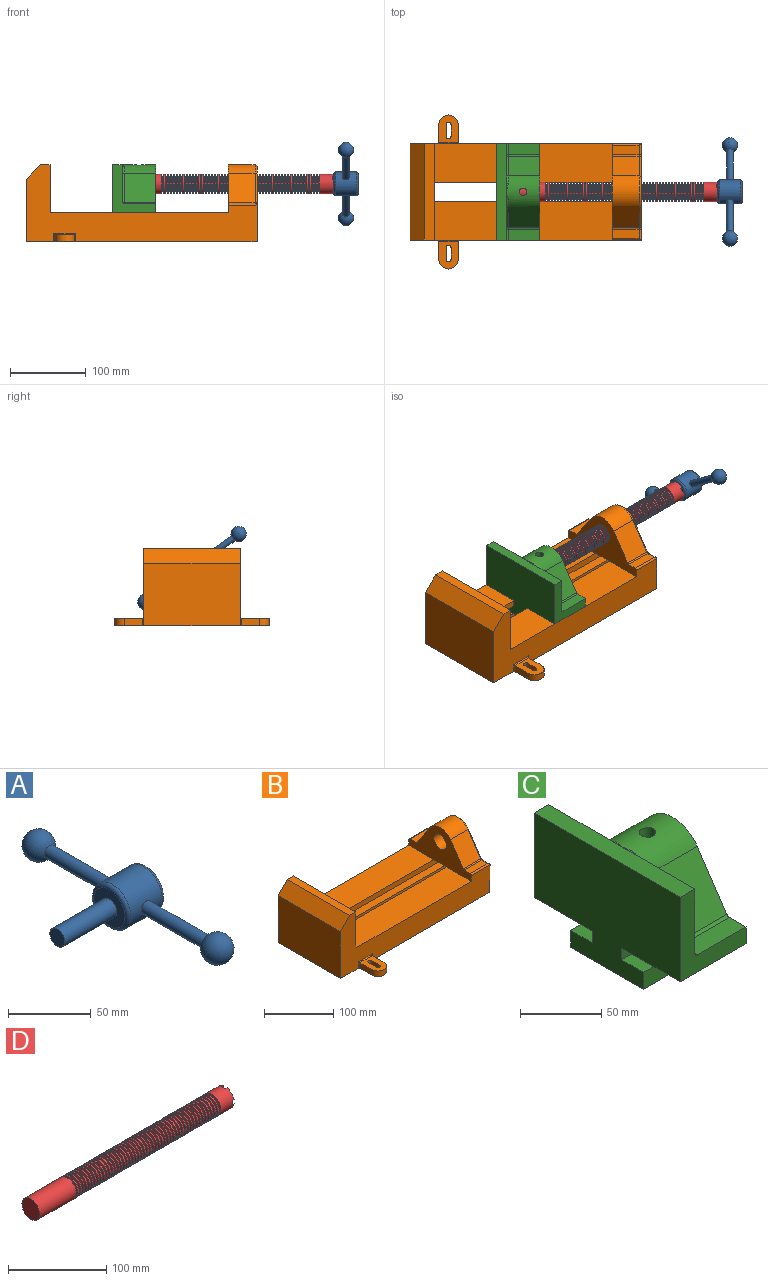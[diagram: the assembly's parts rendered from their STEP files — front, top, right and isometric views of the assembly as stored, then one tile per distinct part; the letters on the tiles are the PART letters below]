
ASSEMBLY  parts=4 mates=4
PART A: 11 faces, bbox 76.2x172.7x34.4 mm
  f0: sphere r=10.16mm, area 1231.8mm2, adj f1
  f1: cylinder r=4.45mm len=51.82mm, axis (0,1,0), area 1438.5mm2, adj f0,f4
  f2: sphere r=10.16mm, area 1231.8mm2, adj f3
  f3: cylinder r=4.45mm len=51.82mm, axis (0,1,0), area 1438.5mm2, adj f2,f4
  f4: cylinder r=15.88mm len=31.75mm, axis (-1,0,0), area 2534.7mm2, adj f1,f3,f9,f10
  f5: cylinder r=6.35mm len=44.45mm, axis (-1,0,0), area 1773.5mm2, adj f6,f8
  f6: plane 12.7x12.7mm, normal (-1,0,0), area 126.7mm2, adj f5
  f7: plane 26.67x26.67mm, normal (1,0,0), area 558.6mm2, adj f10
  f8: plane 26.67x26.67mm, normal (-1,0,0), area 432mm2, adj f5,f9
  f9: torus R=13.33mm, axis (1,0,0), area 374.8mm2, adj f4,f8
  f10: torus R=13.33mm, axis (1,0,0), area 374.8mm2, adj f4,f7
PART B: 61 faces, bbox 304.8x203.2x103.7 mm
  f0: plane 304.8x101.6mm, normal (0,1,0), area 13520.3mm2, adj f3,f4,f5,f6,f7,f8,f9,f16
  f1: plane 304.8x101.6mm, normal (0,-1,0), area 13520.3mm2, adj f2,f3,f5,f6,f7,f8,f9,f16
  f2: plane 234.95x50.8mm, normal (0,0,1), area 11935.5mm2, adj f1,f5,f16,f26
  f3: plane 127x99.06mm, normal (1,0,0), area 7097.5mm2, adj f0,f1,f9,f14,f17,f18,f19,f20
  f4: plane 234.95x50.8mm, normal (0,0,1), area 11935.5mm2, adj f0,f5,f16,f27
  f5: plane 127x101.6mm, normal (1,0,0), area 9516.1mm2, adj f0,f1,f2,f4,f6,f9,f18,f19
  f6: plane 127x12.7mm, normal (0,0,1), area 1612.9mm2, adj f0,f1,f5,f7
  f7: plane 127x19.05mm, normal (-0.71,0,0.71), area 3421.5mm2, adj f0,f1,f6,f8
  f8: plane 127x82.55mm, normal (-1,0,0), area 10483.8mm2, adj f0,f1,f7,f9
  f9: plane 304.8x203.2mm, normal (0,0,-1), area 33298.3mm2, adj f0,f1,f3,f5,f8,f21,f22,f39
  f10: plane 35.56x11.98mm, normal (0,0,1), area 426mm2, adj f16,f28,f29,f30
  f11: plane 38.43x35.56mm, normal (0,0.83,0.56), area 1645.4mm2, adj f12,f16,f29,f32
  f12: cylinder r=25.4mm len=42.19mm, axis (1,0,0), area 1770.2mm2, adj f11,f13,f16,f33
  f13: plane 38.43x35.56mm, normal (0,-0.83,0.56), area 1645.4mm2, adj f12,f16,f34,f35
  f14: cylinder r=12.7mm len=38.1mm, axis (1,0,0), area 3040.2mm2, adj f3,f16
  f15: plane 35.56x11.98mm, normal (0,0,1), area 426mm2, adj f16,f34,f36,f38
  f16: plane 127x63.5mm, normal (-1,0,0), area 4155.5mm2, adj f0,f1,f2,f4,f10,f11,f12,f13
  f17: plane 38.1x25.4mm, normal (0,0,-1), area 967.7mm2, adj f3,f16,f26,f27
  f18: plane 273.05x19.05mm, normal (0,0,-1), area 5201.6mm2, adj f3,f5,f19,f26
  f19: plane 273.05x12.7mm, normal (0,1,0), area 3467.7mm2, adj f3,f5,f18,f20
  f20: plane 273.05x19.05mm, normal (0,0,1), area 5201.6mm2, adj f3,f5,f19,f21
  f21: plane 273.05x16.51mm, normal (0,1,0), area 4508.1mm2, adj f3,f5,f9,f20
  f22: plane 273.05x16.51mm, normal (0,-1,0), area 4508.1mm2, adj f3,f5,f9,f23
  f23: plane 273.05x19.05mm, normal (0,0,1), area 5201.6mm2, adj f3,f5,f22,f24
  f24: plane 273.05x12.7mm, normal (0,-1,0), area 3467.7mm2, adj f3,f5,f23,f25
  f25: plane 273.05x19.05mm, normal (0,0,-1), area 5201.6mm2, adj f3,f5,f24,f27
  f26: plane 273.05x8.89mm, normal (0,1,0), area 2427.4mm2, adj f2,f3,f5,f17,f18
  f27: plane 273.05x8.89mm, normal (0,-1,0), area 2427.4mm2, adj f3,f4,f5,f17,f25
  f28: cylinder r=2.54mm len=38.1mm, axis (1,0,0), area 148.3mm2, adj f0,f10,f16,f30
  f29: cylinder r=2.54mm len=35.56mm, axis (-1,0,0), area 88.5mm2, adj f10,f11,f16,f31
  f30: cylinder r=2.54mm len=14.52mm, axis (0,1,0), area 54.3mm2, adj f3,f10,f28,f31
  f31: torus R=5.08mm, axis (-1,0,0), area 13.5mm2, adj f3,f29,f30,f32
  f32: cylinder r=2.54mm len=39.84mm, axis (0,0.56,-0.83), area 184.6mm2, adj f3,f11,f31,f33
  f33: torus R=22.86mm, axis (-1,0,0), area 191.4mm2, adj f3,f12,f32,f35
  f34: cylinder r=2.54mm len=35.56mm, axis (-1,0,0), area 88.5mm2, adj f13,f15,f16,f37
  f35: cylinder r=2.54mm len=39.84mm, axis (0,0.56,0.83), area 184.6mm2, adj f3,f13,f33,f37
  f36: cylinder r=2.54mm len=38.1mm, axis (-1,0,0), area 148.3mm2, adj f1,f15,f16,f38
  f37: torus R=5.08mm, axis (-1,0,0), area 13.5mm2, adj f3,f34,f35,f38
  f38: cylinder r=2.54mm len=14.52mm, axis (0,1,0), area 54.3mm2, adj f3,f15,f36,f37
  f39: plane 23.88x9.53mm, normal (-1,0,0), area 227.4mm2, adj f9,f45,f46,f60
  f40: plane 23.88x9.53mm, normal (1,0,0), area 227.4mm2, adj f9,f45,f46,f58
  f41: cylinder r=3.3mm len=9.53mm, axis (0,0,-1), area 98.8mm2, adj f9,f42,f44,f46
  f42: plane 15.62x9.53mm, normal (-1,0,0), area 148.8mm2, adj f9,f41,f43,f46
  f43: cylinder r=3.3mm len=9.53mm, axis (0,0,-1), area 98.8mm2, adj f9,f42,f44,f46
  f44: plane 15.62x9.53mm, normal (1,0,0), area 148.8mm2, adj f9,f41,f43,f46
  f45: cylinder r=12.7mm len=25.4mm, axis (0,0,-1), area 380mm2, adj f9,f39,f40,f46
  f46: plane 36.58x25.4mm, normal (0,0,1), area 722.4mm2, adj f39,f40,f41,f42,f43,f44,f45,f59
  f47: plane 23.88x9.53mm, normal (-1,0,0), area 227.4mm2, adj f9,f53,f54,f56
  f48: plane 23.88x9.53mm, normal (1,0,0), area 227.4mm2, adj f9,f53,f54,f55
  f49: cylinder r=3.3mm len=9.53mm, axis (0,0,-1), area 98.8mm2, adj f9,f50,f52,f54
  f50: plane 15.62x9.53mm, normal (-1,0,0), area 148.8mm2, adj f9,f49,f51,f54
  f51: cylinder r=3.3mm len=9.53mm, axis (0,0,-1), area 98.8mm2, adj f9,f50,f52,f54
  f52: plane 15.62x9.53mm, normal (1,0,0), area 148.8mm2, adj f9,f49,f51,f54
  f53: cylinder r=12.7mm len=25.4mm, axis (0,0,-1), area 380mm2, adj f9,f47,f48,f54
  f54: plane 36.58x25.4mm, normal (0,0,1), area 722.4mm2, adj f47,f48,f49,f50,f51,f52,f53,f57
  f55: cylinder r=1.52mm len=11.05mm, axis (0,0,-1), area 24.1mm2, adj f0,f9,f48,f57
  f56: cylinder r=1.52mm len=11.05mm, axis (0,0,1), area 24.1mm2, adj f0,f9,f47,f57
  f57: cylinder r=1.52mm len=28.45mm, axis (1,0,0), area 63.5mm2, adj f0,f54,f55,f56
  f58: cylinder r=1.52mm len=11.05mm, axis (0,0,1), area 24.1mm2, adj f1,f9,f40,f59
  f59: cylinder r=1.52mm len=28.45mm, axis (-1,0,0), area 63.5mm2, adj f1,f46,f58,f60
  f60: cylinder r=1.52mm len=11.05mm, axis (0,0,-1), area 24.1mm2, adj f1,f9,f39,f59
PART C: 36 faces, bbox 57.2x127x89 mm
  f0: plane 57.15x50.8mm, normal (0,0,-1), area 2903.2mm2, adj f6,f9,f10,f23
  f1: cylinder r=12.7mm len=44.45mm, axis (1,0,0), area 3464.3mm2, adj f6,f15,f16
  f2: plane 41.91x14.52mm, normal (0,0,1), area 608.5mm2, adj f6,f11,f24,f25
  f3: plane 51.86x48.26mm, normal (1,0,0), area 1495.7mm2, adj f8,f10,f31,f33,f35
  f4: plane 51.86x48.26mm, normal (1,0,0), area 1495.7mm2, adj f8,f11,f24,f28,f29
  f5: plane 57.15x50.8mm, normal (0,0,-1), area 2903.2mm2, adj f6,f9,f11,f22
  f6: plane 127x85.09mm, normal (1,0,0), area 5190.6mm2, adj f0,f1,f2,f5,f7,f10,f11,f12
  f7: plane 41.91x14.52mm, normal (0,0,1), area 608.5mm2, adj f6,f10,f30,f31
  f8: plane 127x12.7mm, normal (0,0,1), area 1612.9mm2, adj f3,f4,f9,f10,f11,f26,f34
  f9: plane 127x85.09mm, normal (-1,0,0), area 9096.8mm2, adj f0,f5,f8,f10,f11,f17,f18,f19
  f10: plane 63.5x57.15mm, normal (0,-1,0), area 1372.3mm2, adj f0,f3,f6,f7,f8,f9,f31
  f11: plane 63.5x57.15mm, normal (0,1,0), area 1372.3mm2, adj f2,f4,f5,f6,f8,f9,f24
  f12: plane 41.91x38.43mm, normal (0,-0.83,0.56), area 1939.2mm2, adj f6,f13,f30,f33
  f13: cylinder r=25.4mm len=44.45mm, axis (1,0,0), area 2026.5mm2, adj f6,f12,f14,f16,f26,f28,f34,f35
  f14: plane 41.91x38.43mm, normal (0,0.83,0.56), area 1939.2mm2, adj f6,f13,f25,f29
  f15: plane 25.4x25.4mm, normal (1,0,0), area 506.7mm2, adj f1
  f16: cylinder r=5.08mm len=13.76mm, axis (0,0,1), area 414mm2, adj f1,f13
  f17: plane 57.15x19.05mm, normal (0,0,1), area 1088.7mm2, adj f6,f9,f18,f23
  f18: plane 57.15x12.7mm, normal (0,-1,0), area 725.8mm2, adj f6,f9,f17,f19
  f19: plane 63.5x57.15mm, normal (0,0,-1), area 3629mm2, adj f6,f9,f18,f20
  f20: plane 57.15x12.7mm, normal (0,1,0), area 725.8mm2, adj f6,f9,f19,f21
  f21: plane 57.15x19.05mm, normal (0,0,1), area 1088.7mm2, adj f6,f9,f20,f22
  f22: plane 57.15x8.89mm, normal (0,1,0), area 508.1mm2, adj f5,f6,f9,f21
  f23: plane 57.15x8.89mm, normal (0,-1,0), area 508.1mm2, adj f0,f6,f9,f17
  f24: cylinder r=2.54mm len=14.52mm, axis (0,-1,0), area 57.9mm2, adj f2,f4,f11,f27
  f25: cylinder r=2.54mm len=41.91mm, axis (1,0,0), area 104.3mm2, adj f2,f6,f14,f27
  f26: bspline ~12.24x2.8mm, area 20.9mm2, adj f8,f13,f28
  f27: sphere r=2.54mm, area 6.3mm2, adj f24,f25,f29
  f28: torus R=27.94mm, axis (1,0,0), area 57.8mm2, adj f4,f13,f26,f29
  f29: cylinder r=2.54mm len=39.84mm, axis (0,-0.56,0.83), area 184.6mm2, adj f4,f14,f27,f28
  f30: cylinder r=2.54mm len=41.91mm, axis (1,0,0), area 104.3mm2, adj f6,f7,f12,f32
  f31: cylinder r=2.54mm len=14.52mm, axis (0,-1,0), area 57.9mm2, adj f3,f7,f10,f32
  f32: sphere r=2.54mm, area 6.3mm2, adj f30,f31,f33
  f33: cylinder r=2.54mm len=39.84mm, axis (0,-0.56,-0.83), area 184.6mm2, adj f3,f12,f32,f35
  f34: bspline ~12.24x2.8mm, area 20.9mm2, adj f8,f13,f35
  f35: torus R=27.94mm, axis (1,0,0), area 57.8mm2, adj f3,f13,f33,f34
PART D: 220 faces, bbox 279.4x25.4x25.4 mm
  f0: cylinder r=12.7mm len=25.4mm, axis (-1,0,0), area 1468.2mm2, adj f1,f2,f3,f5,f7,f208,f209,f210
  f1: plane 9.9x9.9mm, normal (1,0,0), area 62.3mm2, adj f0,f4,f213,f216
  f2: plane 9.9x9.9mm, normal (1,0,0), area 62.3mm2, adj f0,f4,f210,f218
  f3: plane 9.9x9.9mm, normal (1,0,0), area 62.3mm2, adj f0,f4,f209,f212
  f4: cylinder r=6.35mm len=25.4mm, axis (1,0,0), area 960.3mm2, adj f1,f2,f3,f5,f6,f208,f209,f210
  f5: plane 9.9x9.9mm, normal (1,0,0), area 62.3mm2, adj f0,f4,f215,f217
  f6: plane 12.7x12.7mm, normal (1,0,0), area 126.7mm2, adj f4
  f7: cone r=12.7mm half-angle=76deg, axis (1,0,0), area 188mm2, adj f0,f9
  f8: cone r=10.16mm half-angle=76deg, axis (-1,0,0), area 188mm2, adj f9,f10
  f9: cylinder r=10.16mm len=20.32mm, axis (1,0,0), area 81.1mm2, adj f7,f8
  f10: cylinder r=12.7mm len=25.4mm, axis (-1,0,0), area 131.7mm2, adj f8,f11
  f11: cone r=12.7mm half-angle=76deg, axis (1,0,0), area 188mm2, adj f10,f13
  f12: cone r=10.16mm half-angle=76deg, axis (-1,0,0), area 188mm2, adj f13,f14
  f13: cylinder r=10.16mm len=20.32mm, axis (1,0,0), area 81.1mm2, adj f11,f12
  f14: cylinder r=12.7mm len=25.4mm, axis (-1,0,0), area 131.7mm2, adj f12,f15
  f15: cone r=12.7mm half-angle=76deg, axis (1,0,0), area 188mm2, adj f14,f17
  f16: cone r=10.16mm half-angle=76deg, axis (-1,0,0), area 188mm2, adj f17,f18
  f17: cylinder r=10.16mm len=20.32mm, axis (1,0,0), area 81.1mm2, adj f15,f16
  f18: cylinder r=12.7mm len=25.4mm, axis (-1,0,0), area 131.7mm2, adj f16,f19
  f19: cone r=12.7mm half-angle=76deg, axis (1,0,0), area 188mm2, adj f18,f21
  f20: cone r=10.16mm half-angle=76deg, axis (-1,0,0), area 188mm2, adj f21,f22
  f21: cylinder r=10.16mm len=20.32mm, axis (1,0,0), area 81.1mm2, adj f19,f20
  f22: cylinder r=12.7mm len=25.4mm, axis (-1,0,0), area 131.7mm2, adj f20,f23
  f23: cone r=12.7mm half-angle=76deg, axis (1,0,0), area 188mm2, adj f22,f25
  f24: cone r=10.16mm half-angle=76deg, axis (-1,0,0), area 188mm2, adj f25,f26
  f25: cylinder r=10.16mm len=20.32mm, axis (1,0,0), area 81.1mm2, adj f23,f24
  f26: cylinder r=12.7mm len=25.4mm, axis (-1,0,0), area 131.7mm2, adj f24,f27
  f27: cone r=12.7mm half-angle=76deg, axis (1,0,0), area 188mm2, adj f26,f29
  f28: cone r=10.16mm half-angle=76deg, axis (-1,0,0), area 188mm2, adj f29,f30
  f29: cylinder r=10.16mm len=20.32mm, axis (1,0,0), area 81.1mm2, adj f27,f28
  f30: cylinder r=12.7mm len=25.4mm, axis (-1,0,0), area 131.7mm2, adj f28,f31
  f31: cone r=12.7mm half-angle=76deg, axis (1,0,0), area 188mm2, adj f30,f33
  f32: cone r=10.16mm half-angle=76deg, axis (-1,0,0), area 188mm2, adj f33,f34
  f33: cylinder r=10.16mm len=20.32mm, axis (1,0,0), area 81.1mm2, adj f31,f32
  f34: cylinder r=12.7mm len=25.4mm, axis (-1,0,0), area 131.7mm2, adj f32,f35
  f35: cone r=12.7mm half-angle=76deg, axis (1,0,0), area 188mm2, adj f34,f37
  f36: cone r=10.16mm half-angle=76deg, axis (-1,0,0), area 188mm2, adj f37,f38
  f37: cylinder r=10.16mm len=20.32mm, axis (1,0,0), area 81.1mm2, adj f35,f36
  f38: cylinder r=12.7mm len=25.4mm, axis (-1,0,0), area 131.7mm2, adj f36,f39
  f39: cone r=12.7mm half-angle=76deg, axis (1,0,0), area 188mm2, adj f38,f41
  f40: cone r=10.16mm half-angle=76deg, axis (-1,0,0), area 188mm2, adj f41,f42
  f41: cylinder r=10.16mm len=20.32mm, axis (1,0,0), area 81.1mm2, adj f39,f40
  f42: cylinder r=12.7mm len=25.4mm, axis (-1,0,0), area 131.7mm2, adj f40,f43
  f43: cone r=12.7mm half-angle=76deg, axis (1,0,0), area 188mm2, adj f42,f45
  f44: cone r=10.16mm half-angle=76deg, axis (-1,0,0), area 188mm2, adj f45,f46
  f45: cylinder r=10.16mm len=20.32mm, axis (1,0,0), area 81.1mm2, adj f43,f44
  f46: cylinder r=12.7mm len=25.4mm, axis (-1,0,0), area 131.7mm2, adj f44,f47
  f47: cone r=12.7mm half-angle=76deg, axis (1,0,0), area 188mm2, adj f46,f49
  f48: cone r=10.16mm half-angle=76deg, axis (-1,0,0), area 188mm2, adj f49,f50
  f49: cylinder r=10.16mm len=20.32mm, axis (1,0,0), area 81.1mm2, adj f47,f48
  f50: cylinder r=12.7mm len=25.4mm, axis (-1,0,0), area 131.7mm2, adj f48,f51
  f51: cone r=12.7mm half-angle=76deg, axis (1,0,0), area 188mm2, adj f50,f53
  f52: cone r=10.16mm half-angle=76deg, axis (-1,0,0), area 188mm2, adj f53,f54
  f53: cylinder r=10.16mm len=20.32mm, axis (1,0,0), area 81.1mm2, adj f51,f52
  f54: cylinder r=12.7mm len=25.4mm, axis (-1,0,0), area 131.7mm2, adj f52,f55
  f55: cone r=12.7mm half-angle=76deg, axis (1,0,0), area 188mm2, adj f54,f57
  f56: cone r=10.16mm half-angle=76deg, axis (-1,0,0), area 188mm2, adj f57,f58
  f57: cylinder r=10.16mm len=20.32mm, axis (1,0,0), area 81.1mm2, adj f55,f56
  f58: cylinder r=12.7mm len=25.4mm, axis (-1,0,0), area 131.7mm2, adj f56,f59
  f59: cone r=12.7mm half-angle=76deg, axis (1,0,0), area 188mm2, adj f58,f61
  f60: cone r=10.16mm half-angle=76deg, axis (-1,0,0), area 188mm2, adj f61,f62
  f61: cylinder r=10.16mm len=20.32mm, axis (1,0,0), area 81.1mm2, adj f59,f60
  f62: cylinder r=12.7mm len=25.4mm, axis (-1,0,0), area 131.7mm2, adj f60,f63
  f63: cone r=12.7mm half-angle=76deg, axis (1,0,0), area 188mm2, adj f62,f65
  f64: cone r=10.16mm half-angle=76deg, axis (-1,0,0), area 188mm2, adj f65,f66
  f65: cylinder r=10.16mm len=20.32mm, axis (1,0,0), area 81.1mm2, adj f63,f64
  f66: cylinder r=12.7mm len=25.4mm, axis (-1,0,0), area 131.7mm2, adj f64,f67
  f67: cone r=12.7mm half-angle=76deg, axis (1,0,0), area 188mm2, adj f66,f69
  f68: cone r=10.16mm half-angle=76deg, axis (-1,0,0), area 188mm2, adj f69,f70
  f69: cylinder r=10.16mm len=20.32mm, axis (1,0,0), area 81.1mm2, adj f67,f68
  f70: cylinder r=12.7mm len=25.4mm, axis (-1,0,0), area 131.7mm2, adj f68,f71
  f71: cone r=12.7mm half-angle=76deg, axis (1,0,0), area 188mm2, adj f70,f73
  f72: cone r=10.16mm half-angle=76deg, axis (-1,0,0), area 188mm2, adj f73,f74
  f73: cylinder r=10.16mm len=20.32mm, axis (1,0,0), area 81.1mm2, adj f71,f72
  f74: cylinder r=12.7mm len=25.4mm, axis (-1,0,0), area 131.7mm2, adj f72,f75
  f75: cone r=12.7mm half-angle=76deg, axis (1,0,0), area 188mm2, adj f74,f77
  f76: cone r=10.16mm half-angle=76deg, axis (-1,0,0), area 188mm2, adj f77,f78
  f77: cylinder r=10.16mm len=20.32mm, axis (1,0,0), area 81.1mm2, adj f75,f76
  f78: cylinder r=12.7mm len=25.4mm, axis (-1,0,0), area 131.7mm2, adj f76,f79
  f79: cone r=12.7mm half-angle=76deg, axis (1,0,0), area 188mm2, adj f78,f81
  f80: cone r=10.16mm half-angle=76deg, axis (-1,0,0), area 188mm2, adj f81,f82
  f81: cylinder r=10.16mm len=20.32mm, axis (1,0,0), area 81.1mm2, adj f79,f80
  f82: cylinder r=12.7mm len=25.4mm, axis (-1,0,0), area 131.7mm2, adj f80,f83
  f83: cone r=12.7mm half-angle=76deg, axis (1,0,0), area 188mm2, adj f82,f85
  f84: cone r=10.16mm half-angle=76deg, axis (-1,0,0), area 188mm2, adj f85,f86
  f85: cylinder r=10.16mm len=20.32mm, axis (1,0,0), area 81.1mm2, adj f83,f84
  f86: cylinder r=12.7mm len=25.4mm, axis (-1,0,0), area 131.7mm2, adj f84,f87
  f87: cone r=12.7mm half-angle=76deg, axis (1,0,0), area 188mm2, adj f86,f89
  f88: cone r=10.16mm half-angle=76deg, axis (-1,0,0), area 188mm2, adj f89,f90
  f89: cylinder r=10.16mm len=20.32mm, axis (1,0,0), area 81.1mm2, adj f87,f88
  f90: cylinder r=12.7mm len=25.4mm, axis (-1,0,0), area 131.7mm2, adj f88,f91
  f91: cone r=12.7mm half-angle=76deg, axis (1,0,0), area 188mm2, adj f90,f93
  f92: cone r=10.16mm half-angle=76deg, axis (-1,0,0), area 188mm2, adj f93,f94
  f93: cylinder r=10.16mm len=20.32mm, axis (1,0,0), area 81.1mm2, adj f91,f92
  f94: cylinder r=12.7mm len=25.4mm, axis (-1,0,0), area 131.7mm2, adj f92,f95
  f95: cone r=12.7mm half-angle=76deg, axis (1,0,0), area 188mm2, adj f94,f97
  f96: cone r=10.16mm half-angle=76deg, axis (-1,0,0), area 188mm2, adj f97,f98
  f97: cylinder r=10.16mm len=20.32mm, axis (1,0,0), area 81.1mm2, adj f95,f96
  f98: cylinder r=12.7mm len=25.4mm, axis (-1,0,0), area 131.7mm2, adj f96,f99
  f99: cone r=12.7mm half-angle=76deg, axis (1,0,0), area 188mm2, adj f98,f101
  f100: cone r=10.16mm half-angle=76deg, axis (-1,0,0), area 188mm2, adj f101,f102
  f101: cylinder r=10.16mm len=20.32mm, axis (1,0,0), area 81.1mm2, adj f99,f100
  f102: cylinder r=12.7mm len=25.4mm, axis (-1,0,0), area 131.7mm2, adj f100,f103
  f103: cone r=12.7mm half-angle=76deg, axis (1,0,0), area 188mm2, adj f102,f105
  f104: cone r=10.16mm half-angle=76deg, axis (-1,0,0), area 188mm2, adj f105,f106
  f105: cylinder r=10.16mm len=20.32mm, axis (1,0,0), area 81.1mm2, adj f103,f104
  f106: cylinder r=12.7mm len=25.4mm, axis (-1,0,0), area 131.7mm2, adj f104,f107
  f107: cone r=12.7mm half-angle=76deg, axis (1,0,0), area 188mm2, adj f106,f109
  f108: cone r=10.16mm half-angle=76deg, axis (-1,0,0), area 188mm2, adj f109,f110
  f109: cylinder r=10.16mm len=20.32mm, axis (1,0,0), area 81.1mm2, adj f107,f108
  f110: cylinder r=12.7mm len=25.4mm, axis (-1,0,0), area 131.7mm2, adj f108,f111
  f111: cone r=12.7mm half-angle=76deg, axis (1,0,0), area 188mm2, adj f110,f113
  f112: cone r=10.16mm half-angle=76deg, axis (-1,0,0), area 188mm2, adj f113,f114
  f113: cylinder r=10.16mm len=20.32mm, axis (1,0,0), area 81.1mm2, adj f111,f112
  f114: cylinder r=12.7mm len=25.4mm, axis (-1,0,0), area 131.7mm2, adj f112,f115
  f115: cone r=12.7mm half-angle=76deg, axis (1,0,0), area 188mm2, adj f114,f117
  f116: cone r=10.16mm half-angle=76deg, axis (-1,0,0), area 188mm2, adj f117,f118
  f117: cylinder r=10.16mm len=20.32mm, axis (1,0,0), area 81.1mm2, adj f115,f116
  f118: cylinder r=12.7mm len=25.4mm, axis (-1,0,0), area 131.7mm2, adj f116,f119
  f119: cone r=12.7mm half-angle=76deg, axis (1,0,0), area 188mm2, adj f118,f121
  f120: cone r=10.16mm half-angle=76deg, axis (-1,0,0), area 188mm2, adj f121,f122
  f121: cylinder r=10.16mm len=20.32mm, axis (1,0,0), area 81.1mm2, adj f119,f120
  f122: cylinder r=12.7mm len=25.4mm, axis (-1,0,0), area 131.7mm2, adj f120,f123
  f123: cone r=12.7mm half-angle=76deg, axis (1,0,0), area 188mm2, adj f122,f125
  f124: cone r=10.16mm half-angle=76deg, axis (-1,0,0), area 188mm2, adj f125,f126
  f125: cylinder r=10.16mm len=20.32mm, axis (1,0,0), area 81.1mm2, adj f123,f124
  f126: cylinder r=12.7mm len=25.4mm, axis (-1,0,0), area 131.7mm2, adj f124,f127
  f127: cone r=12.7mm half-angle=76deg, axis (1,0,0), area 188mm2, adj f126,f129
  f128: cone r=10.16mm half-angle=76deg, axis (-1,0,0), area 188mm2, adj f129,f130
  f129: cylinder r=10.16mm len=20.32mm, axis (1,0,0), area 81.1mm2, adj f127,f128
  f130: cylinder r=12.7mm len=25.4mm, axis (-1,0,0), area 131.7mm2, adj f128,f131
  f131: cone r=12.7mm half-angle=76deg, axis (1,0,0), area 188mm2, adj f130,f133
  f132: cone r=10.16mm half-angle=76deg, axis (-1,0,0), area 188mm2, adj f133,f134
  f133: cylinder r=10.16mm len=20.32mm, axis (1,0,0), area 81.1mm2, adj f131,f132
  f134: cylinder r=12.7mm len=25.4mm, axis (-1,0,0), area 131.7mm2, adj f132,f135
  f135: cone r=12.7mm half-angle=76deg, axis (1,0,0), area 188mm2, adj f134,f137
  f136: cone r=10.16mm half-angle=76deg, axis (-1,0,0), area 188mm2, adj f137,f138
  f137: cylinder r=10.16mm len=20.32mm, axis (1,0,0), area 81.1mm2, adj f135,f136
  f138: cylinder r=12.7mm len=25.4mm, axis (-1,0,0), area 131.7mm2, adj f136,f139
  f139: cone r=12.7mm half-angle=76deg, axis (1,0,0), area 188mm2, adj f138,f141
  f140: cone r=10.16mm half-angle=76deg, axis (-1,0,0), area 188mm2, adj f141,f142
  f141: cylinder r=10.16mm len=20.32mm, axis (1,0,0), area 81.1mm2, adj f139,f140
  f142: cylinder r=12.7mm len=25.4mm, axis (-1,0,0), area 131.7mm2, adj f140,f143
  f143: cone r=12.7mm half-angle=76deg, axis (1,0,0), area 188mm2, adj f142,f145
  f144: cone r=10.16mm half-angle=76deg, axis (-1,0,0), area 188mm2, adj f145,f146
  f145: cylinder r=10.16mm len=20.32mm, axis (1,0,0), area 81.1mm2, adj f143,f144
  f146: cylinder r=12.7mm len=25.4mm, axis (-1,0,0), area 131.7mm2, adj f144,f147
  f147: cone r=12.7mm half-angle=76deg, axis (1,0,0), area 188mm2, adj f146,f149
  f148: cone r=10.16mm half-angle=76deg, axis (-1,0,0), area 188mm2, adj f149,f150
  f149: cylinder r=10.16mm len=20.32mm, axis (1,0,0), area 81.1mm2, adj f147,f148
  f150: cylinder r=12.7mm len=25.4mm, axis (-1,0,0), area 131.7mm2, adj f148,f151
  f151: cone r=12.7mm half-angle=76deg, axis (1,0,0), area 188mm2, adj f150,f153
  f152: cone r=10.16mm half-angle=76deg, axis (-1,0,0), area 188mm2, adj f153,f154
  f153: cylinder r=10.16mm len=20.32mm, axis (1,0,0), area 81.1mm2, adj f151,f152
  f154: cylinder r=12.7mm len=25.4mm, axis (-1,0,0), area 131.7mm2, adj f152,f155
  f155: cone r=12.7mm half-angle=76deg, axis (1,0,0), area 188mm2, adj f154,f157
  f156: cone r=10.16mm half-angle=76deg, axis (-1,0,0), area 188mm2, adj f157,f158
  f157: cylinder r=10.16mm len=20.32mm, axis (1,0,0), area 81.1mm2, adj f155,f156
  f158: cylinder r=12.7mm len=25.4mm, axis (-1,0,0), area 131.7mm2, adj f156,f159
  f159: cone r=12.7mm half-angle=76deg, axis (1,0,0), area 188mm2, adj f158,f161
  f160: cone r=10.16mm half-angle=76deg, axis (-1,0,0), area 188mm2, adj f161,f162
  f161: cylinder r=10.16mm len=20.32mm, axis (1,0,0), area 81.1mm2, adj f159,f160
  f162: cylinder r=12.7mm len=25.4mm, axis (-1,0,0), area 131.7mm2, adj f160,f163
  f163: cone r=12.7mm half-angle=76deg, axis (1,0,0), area 188mm2, adj f162,f165
  f164: cone r=10.16mm half-angle=76deg, axis (-1,0,0), area 188mm2, adj f165,f166
  f165: cylinder r=10.16mm len=20.32mm, axis (1,0,0), area 81.1mm2, adj f163,f164
  f166: cylinder r=12.7mm len=25.4mm, axis (-1,0,0), area 131.7mm2, adj f164,f167
  f167: cone r=12.7mm half-angle=76deg, axis (1,0,0), area 188mm2, adj f166,f169
  f168: cone r=10.16mm half-angle=76deg, axis (-1,0,0), area 188mm2, adj f169,f170
  f169: cylinder r=10.16mm len=20.32mm, axis (1,0,0), area 81.1mm2, adj f167,f168
  f170: cylinder r=12.7mm len=25.4mm, axis (-1,0,0), area 131.7mm2, adj f168,f171
  f171: cone r=12.7mm half-angle=76deg, axis (1,0,0), area 188mm2, adj f170,f173
  f172: cone r=10.16mm half-angle=76deg, axis (-1,0,0), area 188mm2, adj f173,f174
  f173: cylinder r=10.16mm len=20.32mm, axis (1,0,0), area 81.1mm2, adj f171,f172
  f174: cylinder r=12.7mm len=25.4mm, axis (-1,0,0), area 131.7mm2, adj f172,f175
  f175: cone r=12.7mm half-angle=76deg, axis (1,0,0), area 188mm2, adj f174,f177
  f176: cone r=10.16mm half-angle=76deg, axis (-1,0,0), area 188mm2, adj f177,f178
  f177: cylinder r=10.16mm len=20.32mm, axis (1,0,0), area 81.1mm2, adj f175,f176
  f178: cylinder r=12.7mm len=25.4mm, axis (-1,0,0), area 131.7mm2, adj f176,f179
  f179: cone r=12.7mm half-angle=76deg, axis (1,0,0), area 188mm2, adj f178,f181
  f180: cone r=10.16mm half-angle=76deg, axis (-1,0,0), area 188mm2, adj f181,f182
  f181: cylinder r=10.16mm len=20.32mm, axis (1,0,0), area 81.1mm2, adj f179,f180
  f182: cylinder r=12.7mm len=25.4mm, axis (-1,0,0), area 131.7mm2, adj f180,f183
  f183: cone r=12.7mm half-angle=76deg, axis (1,0,0), area 188mm2, adj f182,f185
  f184: cone r=10.16mm half-angle=76deg, axis (-1,0,0), area 188mm2, adj f185,f186
  f185: cylinder r=10.16mm len=20.32mm, axis (1,0,0), area 81.1mm2, adj f183,f184
  f186: cylinder r=12.7mm len=25.4mm, axis (-1,0,0), area 131.7mm2, adj f184,f187
  f187: cone r=12.7mm half-angle=76deg, axis (1,0,0), area 188mm2, adj f186,f189
  f188: cone r=10.16mm half-angle=76deg, axis (-1,0,0), area 188mm2, adj f189,f190
  f189: cylinder r=10.16mm len=20.32mm, axis (1,0,0), area 81.1mm2, adj f187,f188
  f190: cylinder r=12.7mm len=25.4mm, axis (-1,0,0), area 131.7mm2, adj f188,f191
  f191: cone r=12.7mm half-angle=76deg, axis (1,0,0), area 188mm2, adj f190,f193
  f192: cone r=10.16mm half-angle=76deg, axis (-1,0,0), area 188mm2, adj f193,f194
  f193: cylinder r=10.16mm len=20.32mm, axis (1,0,0), area 81.1mm2, adj f191,f192
  f194: cylinder r=12.7mm len=25.4mm, axis (-1,0,0), area 131.7mm2, adj f192,f195
  f195: cone r=12.7mm half-angle=76deg, axis (1,0,0), area 188mm2, adj f194,f197
  f196: cone r=10.16mm half-angle=76deg, axis (-1,0,0), area 188mm2, adj f197,f198
  f197: cylinder r=10.16mm len=20.32mm, axis (1,0,0), area 81.1mm2, adj f195,f196
  f198: cylinder r=12.7mm len=25.4mm, axis (-1,0,0), area 131.7mm2, adj f196,f199
  f199: cone r=12.7mm half-angle=76deg, axis (1,0,0), area 188mm2, adj f198,f201
  f200: cone r=10.16mm half-angle=76deg, axis (-1,0,0), area 188mm2, adj f201,f202
  f201: cylinder r=10.16mm len=20.32mm, axis (1,0,0), area 81.1mm2, adj f199,f200
  f202: cylinder r=12.7mm len=25.4mm, axis (-1,0,0), area 131.7mm2, adj f200,f203
  f203: cone r=12.7mm half-angle=76deg, axis (1,0,0), area 188mm2, adj f202,f205
  f204: cone r=10.16mm half-angle=76deg, axis (-1,0,0), area 188mm2, adj f205,f207
  f205: cylinder r=10.16mm len=20.32mm, axis (1,0,0), area 81.1mm2, adj f203,f204
  f206: plane 25.4x25.4mm, normal (-1,0,0), area 506.7mm2, adj f207
  f207: cylinder r=12.7mm len=52.45mm, axis (-1,0,0), area 4185.4mm2, adj f204,f206
  f208: plane 6.88x5.08mm, normal (1,0,0), area 32.7mm2, adj f0,f4,f209,f210
  f209: plane 6.62x2.54mm, normal (0,-1,0), area 16.8mm2, adj f0,f3,f4,f208
  f210: plane 6.62x2.54mm, normal (0,1,0), area 16.8mm2, adj f0,f2,f4,f208
  f211: plane 6.88x5.08mm, normal (1,0,0), area 32.7mm2, adj f0,f4,f212,f213
  f212: plane 6.62x2.54mm, normal (0,0,1), area 16.8mm2, adj f0,f3,f4,f211
  f213: plane 6.62x2.54mm, normal (0,0,-1), area 16.8mm2, adj f0,f1,f4,f211
  f214: plane 6.88x5.08mm, normal (1,0,0), area 32.7mm2, adj f0,f4,f215,f216
  f215: plane 6.62x2.54mm, normal (0,1,0), area 16.8mm2, adj f0,f4,f5,f214
  f216: plane 6.62x2.54mm, normal (0,-1,0), area 16.8mm2, adj f0,f1,f4,f214
  f217: plane 6.62x2.54mm, normal (0,0,-1), area 16.8mm2, adj f0,f4,f5,f219
  f218: plane 6.62x2.54mm, normal (0,0,1), area 16.8mm2, adj f0,f2,f4,f219
  f219: plane 6.88x5.08mm, normal (1,0,0), area 32.7mm2, adj f0,f4,f217,f218
PLACE A rot(axis=(1,0,0),143.9deg) t=(63.37,44.85,137.8)mm
PLACE B at identity fixed
PLACE C t=(82.42,0,0)mm
PLACE D rot(axis=(1,0,0),143.9deg) t=(82.42,44.85,137.8)mm
MATE fastened A.f5 <-> D.f4  axis (-1,0,0) through (101.47,0,76.2)mm
MATE revolute D.f7 <-> C.f28  axis (-1,0,0) through (-177.93,0,76.2)mm
MATE slider C.f9 <-> B.f5  axis (-1,0,0) through (-190.63,-63.5,38.1)mm
MATE cylindrical B.f12 <-> D.f7  axis (1,0,0) through (-19.05,0,76.2)mm
